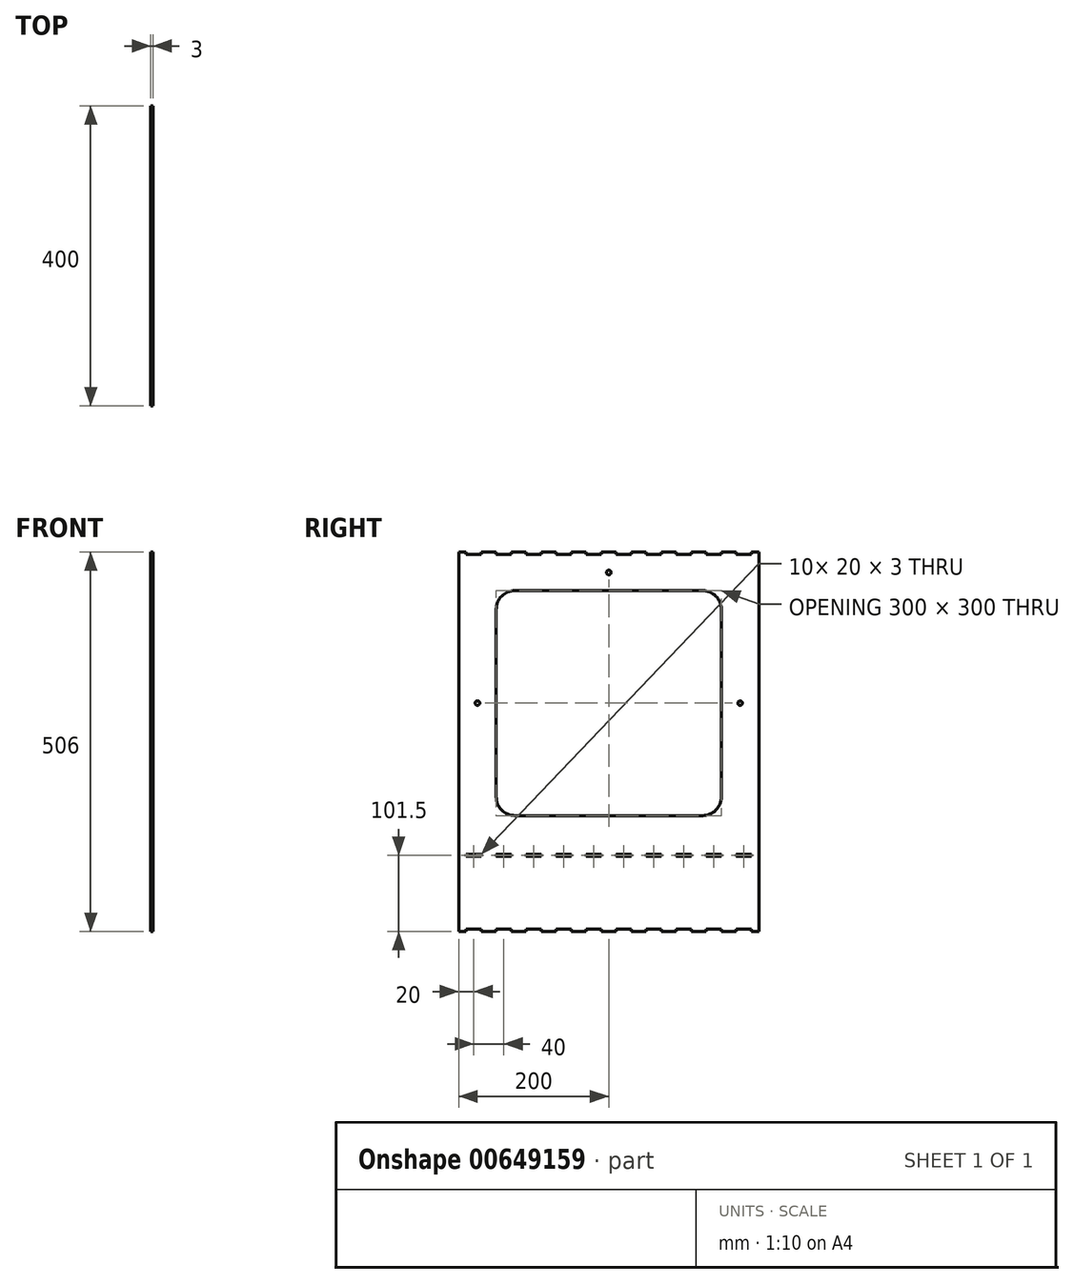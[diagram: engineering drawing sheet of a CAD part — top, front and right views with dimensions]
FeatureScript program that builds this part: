
annotation { "Feature Type Name" : "Feature", "Feature Type Description" : "" }
export const myFeature = defineFeature(function(context is Context, id is Id, definition is map)
    precondition{}
    {
        {
            var Q0;
            Q0=qCreatedBy(makeId("Right.planeOp"),FACE);
            var sketch = newSketch(context, id + "F0", { "sketchPlane" : qUnion([Q0])});
            skLineSegment(sketch, "E0.bottom", {"start": v(200, 250) * mm, "end": v(-200, 250) * mm});
            skLineSegment(sketch, "E0.top", {"start": v(200, -250) * mm, "end": v(-200, -250) * mm});
            skLineSegment(sketch, "E0.left", {"start": v(200, 250) * mm, "end": v(200, -250) * mm});
            skLineSegment(sketch, "E0.right", {"start": v(-200, 250) * mm, "end": v(-200, -250) * mm});
            skPoint(sketch, "E0.middle", {"position": v(0, 0) * mm});
            skSolve(sketch);
        }
        {
            var Q0;
            Q0 = qSketchRegion(id + "F0", true);
            extrude(context, id + "F1", {"entities" : qUnion([Q0]), "depth" : 3 * mm, "offsetDistance" : 25 * mm});
        }
        {
            var Q0;
            Q0=makeQuery(id+"F1.opExtrude","CAP_FACE",FACE,{"disambiguationData":[OSD([sQuery(id+"F0.wireOp",EDGE,"E0.bottom"),sQuery(id+"F0.wireOp",EDGE,"E0.top"),sQuery(id+"F0.wireOp",EDGE,"E0.left"),sQuery(id+"F0.wireOp",EDGE,"E0.right")])],"isStart":false});
            var sketch = newSketch(context, id + "F2", { "sketchPlane" : qUnion([Q0])});
            skLineSegment(sketch, "E1.bottom", {"start": v(-200, 250) * mm, "end": v(-190, 250) * mm});
            skLineSegment(sketch, "E1.top", {"start": v(-200, 253) * mm, "end": v(-190, 253) * mm});
            skLineSegment(sketch, "E1.left", {"start": v(-200, 250) * mm, "end": v(-200, 253) * mm});
            skLineSegment(sketch, "E1.right", {"start": v(-190, 250) * mm, "end": v(-190, 253) * mm});
            skLineSegment(sketch, "E2", {"start": v(-190, 250) * mm, "end": v(-170, 250) * mm, "construction": true});
            skLineSegment(sketch, "E3.bottom", {"start": v(-170, 250) * mm, "end": v(-150, 250) * mm});
            skLineSegment(sketch, "E3.top", {"start": v(-170, 253) * mm, "end": v(-150, 253) * mm});
            skLineSegment(sketch, "E3.left", {"start": v(-170, 250) * mm, "end": v(-170, 253) * mm});
            skLineSegment(sketch, "E3.right", {"start": v(-150, 250) * mm, "end": v(-150, 253) * mm});
            skLineSegment(sketch, "E4.1.0.0", {"start": v(-110, 250) * mm, "end": v(-110, 253) * mm});
            skLineSegment(sketch, "E4.1.0.1", {"start": v(-130, 250) * mm, "end": v(-110, 250) * mm});
            skLineSegment(sketch, "E4.1.0.2", {"start": v(-130, 250) * mm, "end": v(-130, 253) * mm});
            skLineSegment(sketch, "E4.1.0.3", {"start": v(-130, 253) * mm, "end": v(-110, 253) * mm});
            skLineSegment(sketch, "E4.2.0.0", {"start": v(-70, 250) * mm, "end": v(-70, 253) * mm});
            skLineSegment(sketch, "E4.2.0.1", {"start": v(-90, 250) * mm, "end": v(-70, 250) * mm});
            skLineSegment(sketch, "E4.2.0.2", {"start": v(-90, 250) * mm, "end": v(-90, 253) * mm});
            skLineSegment(sketch, "E4.2.0.3", {"start": v(-90, 253) * mm, "end": v(-70, 253) * mm});
            skLineSegment(sketch, "E4.3.0.0", {"start": v(-30, 250) * mm, "end": v(-30, 253) * mm});
            skLineSegment(sketch, "E4.3.0.1", {"start": v(-50, 250) * mm, "end": v(-30, 250) * mm});
            skLineSegment(sketch, "E4.3.0.2", {"start": v(-50, 250) * mm, "end": v(-50, 253) * mm});
            skLineSegment(sketch, "E4.3.0.3", {"start": v(-50, 253) * mm, "end": v(-30, 253) * mm});
            skLineSegment(sketch, "E4.4.0.0", {"start": v(10, 250) * mm, "end": v(10, 253) * mm});
            skLineSegment(sketch, "E4.4.0.1", {"start": v(-10, 250) * mm, "end": v(10, 250) * mm});
            skLineSegment(sketch, "E4.4.0.2", {"start": v(-10, 250) * mm, "end": v(-10, 253) * mm});
            skLineSegment(sketch, "E4.4.0.3", {"start": v(-10, 253) * mm, "end": v(10, 253) * mm});
            skLineSegment(sketch, "E4.5.0.0", {"start": v(50, 250) * mm, "end": v(50, 253) * mm});
            skLineSegment(sketch, "E4.5.0.1", {"start": v(30, 250) * mm, "end": v(50, 250) * mm});
            skLineSegment(sketch, "E4.5.0.2", {"start": v(30, 250) * mm, "end": v(30, 253) * mm});
            skLineSegment(sketch, "E4.5.0.3", {"start": v(30, 253) * mm, "end": v(50, 253) * mm});
            skLineSegment(sketch, "E4.6.0.0", {"start": v(90, 250) * mm, "end": v(90, 253) * mm});
            skLineSegment(sketch, "E4.6.0.1", {"start": v(70, 250) * mm, "end": v(90, 250) * mm});
            skLineSegment(sketch, "E4.6.0.2", {"start": v(70, 250) * mm, "end": v(70, 253) * mm});
            skLineSegment(sketch, "E4.6.0.3", {"start": v(70, 253) * mm, "end": v(90, 253) * mm});
            skLineSegment(sketch, "E4.7.0.0", {"start": v(130, 250) * mm, "end": v(130, 253) * mm});
            skLineSegment(sketch, "E4.7.0.1", {"start": v(110, 250) * mm, "end": v(130, 250) * mm});
            skLineSegment(sketch, "E4.7.0.2", {"start": v(110, 250) * mm, "end": v(110, 253) * mm});
            skLineSegment(sketch, "E4.7.0.3", {"start": v(110, 253) * mm, "end": v(130, 253) * mm});
            skLineSegment(sketch, "E4.8.0.0", {"start": v(170, 250) * mm, "end": v(170, 253) * mm});
            skLineSegment(sketch, "E4.8.0.1", {"start": v(150, 250) * mm, "end": v(170, 250) * mm});
            skLineSegment(sketch, "E4.8.0.2", {"start": v(150, 250) * mm, "end": v(150, 253) * mm});
            skLineSegment(sketch, "E4.8.0.3", {"start": v(150, 253) * mm, "end": v(170, 253) * mm});
            skLineSegment(sketch, "E4.direction1", {"start": v(-170, 250) * mm, "end": v(-130, 250) * mm, "construction": true});
            skLineSegment(sketch, "E5.bottom", {"start": v(200, 250) * mm, "end": v(190, 250) * mm});
            skLineSegment(sketch, "E5.top", {"start": v(200, 253) * mm, "end": v(190, 253) * mm});
            skLineSegment(sketch, "E5.left", {"start": v(200, 250) * mm, "end": v(200, 253) * mm});
            skLineSegment(sketch, "E5.right", {"start": v(190, 250) * mm, "end": v(190, 253) * mm});
            skLineSegment(sketch, "E6.MirrorCS", {"start": v(-190, -250) * mm, "end": v(-190, -253) * mm});
            skLineSegment(sketch, "E7.MirrorCS", {"start": v(-190, -250) * mm, "end": v(-170, -250) * mm, "construction": true});
            skLineSegment(sketch, "E8.MirrorCS", {"start": v(-170, -250) * mm, "end": v(-150, -250) * mm});
            skLineSegment(sketch, "E9.MirrorCS", {"start": v(-170, -253) * mm, "end": v(-150, -253) * mm});
            skLineSegment(sketch, "E10.MirrorCS", {"start": v(-170, -250) * mm, "end": v(-170, -253) * mm});
            skLineSegment(sketch, "E11.MirrorCS", {"start": v(-150, -250) * mm, "end": v(-150, -253) * mm});
            skLineSegment(sketch, "E12.MirrorCS", {"start": v(-130, -250) * mm, "end": v(-130, -253) * mm});
            skLineSegment(sketch, "E13.MirrorCS", {"start": v(200, -250) * mm, "end": v(200, -253) * mm});
            skLineSegment(sketch, "E14.MirrorCS", {"start": v(-90, -250) * mm, "end": v(-90, -253) * mm});
            skLineSegment(sketch, "E15.MirrorCS", {"start": v(-200, -253) * mm, "end": v(-190, -253) * mm});
            skLineSegment(sketch, "E16.MirrorCS", {"start": v(-200, -250) * mm, "end": v(-190, -250) * mm});
            skLineSegment(sketch, "E17.MirrorCS", {"start": v(-200, -250) * mm, "end": v(-200, -253) * mm});
            skLineSegment(sketch, "E18.MirrorCS", {"start": v(-130, -253) * mm, "end": v(-110, -253) * mm});
            skLineSegment(sketch, "E19.MirrorCS", {"start": v(-110, -250) * mm, "end": v(-110, -253) * mm});
            skLineSegment(sketch, "E20.MirrorCS", {"start": v(-130, -250) * mm, "end": v(-110, -250) * mm});
            skLineSegment(sketch, "E21.MirrorCS", {"start": v(200, -253) * mm, "end": v(190, -253) * mm});
            skLineSegment(sketch, "E22.MirrorCS", {"start": v(150, -250) * mm, "end": v(150, -253) * mm});
            skLineSegment(sketch, "E23.MirrorCS", {"start": v(-10, -250) * mm, "end": v(-10, -253) * mm});
            skLineSegment(sketch, "E24.MirrorCS", {"start": v(190, -250) * mm, "end": v(190, -253) * mm});
            skLineSegment(sketch, "E25.MirrorCS", {"start": v(-90, -253) * mm, "end": v(-70, -253) * mm});
            skLineSegment(sketch, "E26.MirrorCS", {"start": v(170, -250) * mm, "end": v(170, -253) * mm});
            skLineSegment(sketch, "E27.MirrorCS", {"start": v(10, -250) * mm, "end": v(10, -253) * mm});
            skLineSegment(sketch, "E28.MirrorCS", {"start": v(130, -250) * mm, "end": v(130, -253) * mm});
            skLineSegment(sketch, "E29.MirrorCS", {"start": v(-30, -250) * mm, "end": v(-30, -253) * mm});
            skLineSegment(sketch, "E30.MirrorCS", {"start": v(-90, -250) * mm, "end": v(-70, -250) * mm});
            skLineSegment(sketch, "E31.MirrorCS", {"start": v(-170, -250) * mm, "end": v(-130, -250) * mm, "construction": true});
            skLineSegment(sketch, "E32.MirrorCS", {"start": v(200, -250) * mm, "end": v(190, -250) * mm});
            skLineSegment(sketch, "E33.MirrorCS", {"start": v(30, -250) * mm, "end": v(30, -253) * mm});
            skLineSegment(sketch, "E34.MirrorCS", {"start": v(90, -250) * mm, "end": v(90, -253) * mm});
            skLineSegment(sketch, "E35.MirrorCS", {"start": v(110, -253) * mm, "end": v(130, -253) * mm});
            skLineSegment(sketch, "E36.MirrorCS", {"start": v(-50, -253) * mm, "end": v(-30, -253) * mm});
            skLineSegment(sketch, "E37.MirrorCS", {"start": v(70, -253) * mm, "end": v(90, -253) * mm});
            skLineSegment(sketch, "E38.MirrorCS", {"start": v(150, -253) * mm, "end": v(170, -253) * mm});
            skLineSegment(sketch, "E39.MirrorCS", {"start": v(30, -253) * mm, "end": v(50, -253) * mm});
            skLineSegment(sketch, "E40.MirrorCS", {"start": v(-10, -253) * mm, "end": v(10, -253) * mm});
            skLineSegment(sketch, "E41.MirrorCS", {"start": v(70, -250) * mm, "end": v(90, -250) * mm});
            skLineSegment(sketch, "E42.MirrorCS", {"start": v(-70, -250) * mm, "end": v(-70, -253) * mm});
            skLineSegment(sketch, "E43.MirrorCS", {"start": v(-50, -250) * mm, "end": v(-50, -253) * mm});
            skLineSegment(sketch, "E44.MirrorCS", {"start": v(150, -250) * mm, "end": v(170, -250) * mm});
            skLineSegment(sketch, "E45.MirrorCS", {"start": v(70, -250) * mm, "end": v(70, -253) * mm});
            skLineSegment(sketch, "E46.MirrorCS", {"start": v(-10, -250) * mm, "end": v(10, -250) * mm});
            skLineSegment(sketch, "E47.MirrorCS", {"start": v(110, -250) * mm, "end": v(130, -250) * mm});
            skLineSegment(sketch, "E48.MirrorCS", {"start": v(-50, -250) * mm, "end": v(-30, -250) * mm});
            skLineSegment(sketch, "E49.MirrorCS", {"start": v(50, -250) * mm, "end": v(50, -253) * mm});
            skLineSegment(sketch, "E50.MirrorCS", {"start": v(30, -250) * mm, "end": v(50, -250) * mm});
            skLineSegment(sketch, "E51.MirrorCS", {"start": v(110, -250) * mm, "end": v(110, -253) * mm});
            skSolve(sketch);
        }
        {
            var Q0;
            Q0 = qSketchRegion(id + "F2", true);
            var Q1;
            Q1=makeQuery(id+"F1.opExtrude","CAP_FACE",FACE,{"disambiguationData":[OSD([sQuery(id+"F0.wireOp",EDGE,"E0.bottom"),sQuery(id+"F0.wireOp",EDGE,"E0.top"),sQuery(id+"F0.wireOp",EDGE,"E0.left"),sQuery(id+"F0.wireOp",EDGE,"E0.right")])],"isStart":true});
            extrude(context, id + "F3", {"entities" : qUnion([Q0]), "operationType" : NewBodyOperationType.ADD, "endBound" : BoundingType.UP_TO_SURFACE, "oppositeDirection" : true, "depth" : 25 * mm, "endBoundEntityFace" : qUnion([Q1]), "offsetDistance" : 25 * mm});
        }
        {
            var Q0;
            {var subQ0=sQuery(id+"F0.wireOp",EDGE,"E0.right");var subQ1=sQuery(id+"F0.wireOp",EDGE,"E0.left");var subQ2=sQuery(id+"F0.wireOp",EDGE,"E0.top");var subQ3=sQuery(id+"F0.wireOp",EDGE,"E0.bottom");Q0=makeQuery(id+"F3.boolean.opBoolean","MERGE",FACE,{"derivedFrom":[makeQuery(id+"F1.opExtrude","CAP_FACE",FACE,{"disambiguationData":[OSD([subQ3,subQ2,subQ1,subQ0])],"isStart":true}),makeQuery(id+"F3.opExtrude","CAP_FACE",FACE,{"disambiguationData":[OSD([subQ3,subQ2,subQ1,subQ0]),OD(0.0)],"isStart":false}),makeQuery(id+"F3.opExtrude","CAP_FACE",FACE,{"disambiguationData":[OSD([subQ3,subQ2,subQ1,subQ0]),OD(1.0)],"isStart":false}),makeQuery(id+"F3.opExtrude","CAP_FACE",FACE,{"disambiguationData":[OSD([subQ3,subQ2,subQ1,subQ0]),OD(2.0)],"isStart":false}),makeQuery(id+"F3.opExtrude","CAP_FACE",FACE,{"disambiguationData":[OSD([subQ3,subQ2,subQ1,subQ0]),OD(3.0)],"isStart":false}),makeQuery(id+"F3.opExtrude","CAP_FACE",FACE,{"disambiguationData":[OSD([subQ3,subQ2,subQ1,subQ0]),OD(4.0)],"isStart":false}),makeQuery(id+"F3.opExtrude","CAP_FACE",FACE,{"disambiguationData":[OSD([subQ3,subQ2,subQ1,subQ0]),OD(5.0)],"isStart":false}),makeQuery(id+"F3.opExtrude","CAP_FACE",FACE,{"disambiguationData":[OSD([subQ3,subQ2,subQ1,subQ0]),OD(6.0)],"isStart":false}),makeQuery(id+"F3.opExtrude","CAP_FACE",FACE,{"disambiguationData":[OSD([subQ3,subQ2,subQ1,subQ0]),OD(7.0)],"isStart":false}),makeQuery(id+"F3.opExtrude","CAP_FACE",FACE,{"disambiguationData":[OSD([subQ3,subQ2,subQ1,subQ0]),OD(8.0)],"isStart":false}),makeQuery(id+"F3.opExtrude","CAP_FACE",FACE,{"disambiguationData":[OSD([subQ3,subQ2,subQ1,subQ0]),OD(9.0)],"isStart":false}),makeQuery(id+"F3.opExtrude","CAP_FACE",FACE,{"disambiguationData":[OSD([subQ3,subQ2,subQ1,subQ0]),OD(10.0)],"isStart":false}),makeQuery(id+"F3.opExtrude","CAP_FACE",FACE,{"disambiguationData":[OSD([subQ3,subQ2,subQ1,subQ0]),OD(11.0)],"isStart":false}),makeQuery(id+"F3.opExtrude","CAP_FACE",FACE,{"disambiguationData":[OSD([subQ3,subQ2,subQ1,subQ0]),OD(12.0)],"isStart":false}),makeQuery(id+"F3.opExtrude","CAP_FACE",FACE,{"disambiguationData":[OSD([subQ3,subQ2,subQ1,subQ0]),OD(13.0)],"isStart":false}),makeQuery(id+"F3.opExtrude","CAP_FACE",FACE,{"disambiguationData":[OSD([subQ3,subQ2,subQ1,subQ0]),OD(14.0)],"isStart":false}),makeQuery(id+"F3.opExtrude","CAP_FACE",FACE,{"disambiguationData":[OSD([subQ3,subQ2,subQ1,subQ0]),OD(15.0)],"isStart":false}),makeQuery(id+"F3.opExtrude","CAP_FACE",FACE,{"disambiguationData":[OSD([subQ3,subQ2,subQ1,subQ0]),OD(16.0)],"isStart":false}),makeQuery(id+"F3.opExtrude","CAP_FACE",FACE,{"disambiguationData":[OSD([subQ3,subQ2,subQ1,subQ0]),OD(17.0)],"isStart":false}),makeQuery(id+"F3.opExtrude","CAP_FACE",FACE,{"disambiguationData":[OSD([subQ3,subQ2,subQ1,subQ0]),OD(18.0)],"isStart":false}),makeQuery(id+"F3.opExtrude","CAP_FACE",FACE,{"disambiguationData":[OSD([subQ3,subQ2,subQ1,subQ0]),OD(19.0)],"isStart":false}),makeQuery(id+"F3.opExtrude","CAP_FACE",FACE,{"disambiguationData":[OSD([subQ3,subQ2,subQ1,subQ0]),OD(20.0)],"isStart":false}),makeQuery(id+"F3.opExtrude","CAP_FACE",FACE,{"disambiguationData":[OSD([subQ3,subQ2,subQ1,subQ0]),OD(21.0)],"isStart":false})]});}
            var sketch = newSketch(context, id + "F4", { "sketchPlane" : qUnion([Q0])});
            skLineSegment(sketch, "E52", {"start": v(-200, 253) * mm, "end": v(-200, -153) * mm, "construction": true});
            skLineSegment(sketch, "E53", {"start": v(-200, -153) * mm, "end": v(-190, -153) * mm, "construction": true});
            skLineSegment(sketch, "E54.bottom", {"start": v(-190, -153) * mm, "end": v(-170, -153) * mm});
            skLineSegment(sketch, "E54.top", {"start": v(-190, -150) * mm, "end": v(-170, -150) * mm});
            skLineSegment(sketch, "E54.left", {"start": v(-190, -153) * mm, "end": v(-190, -150) * mm});
            skLineSegment(sketch, "E54.right", {"start": v(-170, -153) * mm, "end": v(-170, -150) * mm});
            skLineSegment(sketch, "E55.1.0.0", {"start": v(-150, -150) * mm, "end": v(-130, -150) * mm});
            skLineSegment(sketch, "E55.1.0.1", {"start": v(-150, -153) * mm, "end": v(-130, -153) * mm});
            skLineSegment(sketch, "E55.1.0.2", {"start": v(-130, -153) * mm, "end": v(-130, -150) * mm});
            skLineSegment(sketch, "E55.2.0.0", {"start": v(-110, -150) * mm, "end": v(-90, -150) * mm});
            skLineSegment(sketch, "E55.2.0.1", {"start": v(-110, -153) * mm, "end": v(-90, -153) * mm});
            skLineSegment(sketch, "E55.2.0.2", {"start": v(-90, -153) * mm, "end": v(-90, -150) * mm});
            skLineSegment(sketch, "E55.3.0.0", {"start": v(-70, -150) * mm, "end": v(-50, -150) * mm});
            skLineSegment(sketch, "E55.3.0.1", {"start": v(-70, -153) * mm, "end": v(-50, -153) * mm});
            skLineSegment(sketch, "E55.3.0.2", {"start": v(-50, -153) * mm, "end": v(-50, -150) * mm});
            skLineSegment(sketch, "E55.4.0.0", {"start": v(-30, -150) * mm, "end": v(-10, -150) * mm});
            skLineSegment(sketch, "E55.4.0.1", {"start": v(-30, -153) * mm, "end": v(-10, -153) * mm});
            skLineSegment(sketch, "E55.4.0.2", {"start": v(-10, -153) * mm, "end": v(-10, -150) * mm});
            skLineSegment(sketch, "E55.5.0.0", {"start": v(10, -150) * mm, "end": v(30, -150) * mm});
            skLineSegment(sketch, "E55.5.0.1", {"start": v(10, -153) * mm, "end": v(30, -153) * mm});
            skLineSegment(sketch, "E55.5.0.2", {"start": v(30, -153) * mm, "end": v(30, -150) * mm});
            skLineSegment(sketch, "E55.6.0.0", {"start": v(50, -150) * mm, "end": v(70, -150) * mm});
            skLineSegment(sketch, "E55.6.0.1", {"start": v(50, -153) * mm, "end": v(70, -153) * mm});
            skLineSegment(sketch, "E55.6.0.2", {"start": v(70, -153) * mm, "end": v(70, -150) * mm});
            skLineSegment(sketch, "E55.7.0.0", {"start": v(90, -150) * mm, "end": v(110, -150) * mm});
            skLineSegment(sketch, "E55.7.0.1", {"start": v(90, -153) * mm, "end": v(110, -153) * mm});
            skLineSegment(sketch, "E55.7.0.2", {"start": v(110, -153) * mm, "end": v(110, -150) * mm});
            skLineSegment(sketch, "E55.8.0.0", {"start": v(130, -150) * mm, "end": v(150, -150) * mm});
            skLineSegment(sketch, "E55.8.0.1", {"start": v(130, -153) * mm, "end": v(150, -153) * mm});
            skLineSegment(sketch, "E55.8.0.2", {"start": v(150, -153) * mm, "end": v(150, -150) * mm});
            skLineSegment(sketch, "E55.9.0.0", {"start": v(170, -150) * mm, "end": v(190, -150) * mm});
            skLineSegment(sketch, "E55.9.0.1", {"start": v(170, -153) * mm, "end": v(190, -153) * mm});
            skLineSegment(sketch, "E55.9.0.2", {"start": v(190, -153) * mm, "end": v(190, -150) * mm});
            skLineSegment(sketch, "E55.direction1", {"start": v(-190, -150) * mm, "end": v(-150, -150) * mm, "construction": true});
            skLineSegment(sketch, "E56.1.0.0", {"start": v(-150, -153) * mm, "end": v(-150, -150) * mm});
            skLineSegment(sketch, "E56.2.0.0", {"start": v(-110, -153) * mm, "end": v(-110, -150) * mm});
            skLineSegment(sketch, "E56.3.0.0", {"start": v(-70, -153) * mm, "end": v(-70, -150) * mm});
            skLineSegment(sketch, "E56.4.0.0", {"start": v(-30, -153) * mm, "end": v(-30, -150) * mm});
            skLineSegment(sketch, "E56.5.0.0", {"start": v(10, -153) * mm, "end": v(10, -150) * mm});
            skLineSegment(sketch, "E56.6.0.0", {"start": v(50, -153) * mm, "end": v(50, -150) * mm});
            skLineSegment(sketch, "E56.7.0.0", {"start": v(90, -153) * mm, "end": v(90, -150) * mm});
            skLineSegment(sketch, "E56.8.0.0", {"start": v(130, -153) * mm, "end": v(130, -150) * mm});
            skLineSegment(sketch, "E56.9.0.0", {"start": v(170, -153) * mm, "end": v(170, -150) * mm});
            skLineSegment(sketch, "E56.direction1", {"start": v(-190, -153) * mm, "end": v(-150, -153) * mm, "construction": true});
            skSolve(sketch);
        }
        {
            var Q0;
            Q0 = qSketchRegion(id + "F4", true);
            extrude(context, id + "F5", {"entities" : qUnion([Q0]), "operationType" : NewBodyOperationType.REMOVE, "endBound" : BoundingType.THROUGH_ALL, "oppositeDirection" : true, "depth" : 25 * mm, "offsetDistance" : 25 * mm});
        }
        {
            var Q0;
            {var subQ0=sQuery(id+"F0.wireOp",EDGE,"E0.right");var subQ1=sQuery(id+"F0.wireOp",EDGE,"E0.left");var subQ2=sQuery(id+"F0.wireOp",EDGE,"E0.top");var subQ3=sQuery(id+"F0.wireOp",EDGE,"E0.bottom");Q0=makeQuery(id+"F3.boolean.opBoolean","MERGE",FACE,{"derivedFrom":[makeQuery(id+"F1.opExtrude","CAP_FACE",FACE,{"disambiguationData":[OSD([subQ3,subQ2,subQ1,subQ0])],"isStart":true}),makeQuery(id+"F3.opExtrude","CAP_FACE",FACE,{"disambiguationData":[OSD([subQ3,subQ2,subQ1,subQ0]),OD(0.0)],"isStart":false}),makeQuery(id+"F3.opExtrude","CAP_FACE",FACE,{"disambiguationData":[OSD([subQ3,subQ2,subQ1,subQ0]),OD(1.0)],"isStart":false}),makeQuery(id+"F3.opExtrude","CAP_FACE",FACE,{"disambiguationData":[OSD([subQ3,subQ2,subQ1,subQ0]),OD(2.0)],"isStart":false}),makeQuery(id+"F3.opExtrude","CAP_FACE",FACE,{"disambiguationData":[OSD([subQ3,subQ2,subQ1,subQ0]),OD(3.0)],"isStart":false}),makeQuery(id+"F3.opExtrude","CAP_FACE",FACE,{"disambiguationData":[OSD([subQ3,subQ2,subQ1,subQ0]),OD(4.0)],"isStart":false}),makeQuery(id+"F3.opExtrude","CAP_FACE",FACE,{"disambiguationData":[OSD([subQ3,subQ2,subQ1,subQ0]),OD(5.0)],"isStart":false}),makeQuery(id+"F3.opExtrude","CAP_FACE",FACE,{"disambiguationData":[OSD([subQ3,subQ2,subQ1,subQ0]),OD(6.0)],"isStart":false}),makeQuery(id+"F3.opExtrude","CAP_FACE",FACE,{"disambiguationData":[OSD([subQ3,subQ2,subQ1,subQ0]),OD(7.0)],"isStart":false}),makeQuery(id+"F3.opExtrude","CAP_FACE",FACE,{"disambiguationData":[OSD([subQ3,subQ2,subQ1,subQ0]),OD(8.0)],"isStart":false}),makeQuery(id+"F3.opExtrude","CAP_FACE",FACE,{"disambiguationData":[OSD([subQ3,subQ2,subQ1,subQ0]),OD(9.0)],"isStart":false}),makeQuery(id+"F3.opExtrude","CAP_FACE",FACE,{"disambiguationData":[OSD([subQ3,subQ2,subQ1,subQ0]),OD(10.0)],"isStart":false}),makeQuery(id+"F3.opExtrude","CAP_FACE",FACE,{"disambiguationData":[OSD([subQ3,subQ2,subQ1,subQ0]),OD(11.0)],"isStart":false}),makeQuery(id+"F3.opExtrude","CAP_FACE",FACE,{"disambiguationData":[OSD([subQ3,subQ2,subQ1,subQ0]),OD(12.0)],"isStart":false}),makeQuery(id+"F3.opExtrude","CAP_FACE",FACE,{"disambiguationData":[OSD([subQ3,subQ2,subQ1,subQ0]),OD(13.0)],"isStart":false}),makeQuery(id+"F3.opExtrude","CAP_FACE",FACE,{"disambiguationData":[OSD([subQ3,subQ2,subQ1,subQ0]),OD(14.0)],"isStart":false}),makeQuery(id+"F3.opExtrude","CAP_FACE",FACE,{"disambiguationData":[OSD([subQ3,subQ2,subQ1,subQ0]),OD(15.0)],"isStart":false}),makeQuery(id+"F3.opExtrude","CAP_FACE",FACE,{"disambiguationData":[OSD([subQ3,subQ2,subQ1,subQ0]),OD(16.0)],"isStart":false}),makeQuery(id+"F3.opExtrude","CAP_FACE",FACE,{"disambiguationData":[OSD([subQ3,subQ2,subQ1,subQ0]),OD(17.0)],"isStart":false}),makeQuery(id+"F3.opExtrude","CAP_FACE",FACE,{"disambiguationData":[OSD([subQ3,subQ2,subQ1,subQ0]),OD(18.0)],"isStart":false}),makeQuery(id+"F3.opExtrude","CAP_FACE",FACE,{"disambiguationData":[OSD([subQ3,subQ2,subQ1,subQ0]),OD(19.0)],"isStart":false}),makeQuery(id+"F3.opExtrude","CAP_FACE",FACE,{"disambiguationData":[OSD([subQ3,subQ2,subQ1,subQ0]),OD(20.0)],"isStart":false}),makeQuery(id+"F3.opExtrude","CAP_FACE",FACE,{"disambiguationData":[OSD([subQ3,subQ2,subQ1,subQ0]),OD(21.0)],"isStart":false})]});}
            var sketch = newSketch(context, id + "F6", { "sketchPlane" : qUnion([Q0])});
            skLineSegment(sketch, "E57", {"start": v(0, 253) * mm, "end": v(0, -150) * mm, "construction": true});
            skLineSegment(sketch, "E58.bottom", {"start": v(150, 201.5) * mm, "end": v(-150, 201.5) * mm});
            skLineSegment(sketch, "E58.top", {"start": v(150, -98.5) * mm, "end": v(-150, -98.5) * mm});
            skLineSegment(sketch, "E58.left", {"start": v(150, 201.5) * mm, "end": v(150, -98.5) * mm});
            skLineSegment(sketch, "E58.right", {"start": v(-150, 201.5) * mm, "end": v(-150, -98.5) * mm});
            skPoint(sketch, "E58.middle", {"position": v(0, 51.5) * mm});
            skSolve(sketch);
        }
        {
            var Q0;
            Q0 = qSketchRegion(id + "F6", true);
            extrude(context, id + "F7", {"entities" : qUnion([Q0]), "operationType" : NewBodyOperationType.REMOVE, "oppositeDirection" : true, "depth" : 25 * mm, "offsetDistance" : 25 * mm});
        }
        {
            var Q0;
            Q0=makeQuery(id+"F7.boolean.opBoolean","COPY",EDGE,{"derivedFrom":makeQuery(id+"F7.opExtrude","SWEPT_EDGE",EDGE,{"disambiguationData":[OSD([sQuery(id+"F6.wireOp",EDGE,"E58.bottom"),sQuery(id+"F6.wireOp",EDGE,"E58.right")])]})});
            var Q1;
            Q1=makeQuery(id+"F7.boolean.opBoolean","COPY",EDGE,{"derivedFrom":makeQuery(id+"F7.opExtrude","SWEPT_EDGE",EDGE,{"disambiguationData":[OSD([sQuery(id+"F6.wireOp",EDGE,"E58.bottom"),sQuery(id+"F6.wireOp",EDGE,"E58.left")])]})});
            var Q2;
            Q2=makeQuery(id+"F7.boolean.opBoolean","COPY",EDGE,{"derivedFrom":makeQuery(id+"F7.opExtrude","SWEPT_EDGE",EDGE,{"disambiguationData":[OSD([sQuery(id+"F6.wireOp",EDGE,"E58.top"),sQuery(id+"F6.wireOp",EDGE,"E58.left")])]})});
            var Q3;
            Q3=makeQuery(id+"F7.boolean.opBoolean","COPY",EDGE,{"derivedFrom":makeQuery(id+"F7.opExtrude","SWEPT_EDGE",EDGE,{"disambiguationData":[OSD([sQuery(id+"F6.wireOp",EDGE,"E58.top"),sQuery(id+"F6.wireOp",EDGE,"E58.right")])]})});
            fillet(context, id + "F8", {"entities" : qUnion([Q0, Q1, Q2, Q3]), "radius" : 25 * mm, "tangentPropagation" : true, "allowEdgeOverflow" : false});
        }
        {
            var Q0;
            Q0=makeQuery(id+"F3.boolean.opBoolean","MERGE",FACE,{"derivedFrom":[makeQuery(id+"F1.opExtrude","CAP_FACE",FACE,{"disambiguationData":[OSD([sQuery(id+"F0.wireOp",EDGE,"E0.bottom"),sQuery(id+"F0.wireOp",EDGE,"E0.top"),sQuery(id+"F0.wireOp",EDGE,"E0.left"),sQuery(id+"F0.wireOp",EDGE,"E0.right")])],"isStart":false}),makeQuery(id+"F3.opExtrude","CAP_FACE",FACE,{"disambiguationData":[OSD([sQuery(id+"F2.wireOp",EDGE,"E1.bottom"),sQuery(id+"F2.wireOp",EDGE,"E1.top"),sQuery(id+"F2.wireOp",EDGE,"E1.left"),sQuery(id+"F2.wireOp",EDGE,"E1.right")])],"isStart":true}),makeQuery(id+"F3.opExtrude","CAP_FACE",FACE,{"disambiguationData":[OSD([sQuery(id+"F2.wireOp",EDGE,"E3.bottom"),sQuery(id+"F2.wireOp",EDGE,"E3.top"),sQuery(id+"F2.wireOp",EDGE,"E3.left"),sQuery(id+"F2.wireOp",EDGE,"E3.right")])],"isStart":true}),makeQuery(id+"F3.opExtrude","CAP_FACE",FACE,{"disambiguationData":[OSD([sQuery(id+"F2.wireOp",EDGE,"E4.1.0.0"),sQuery(id+"F2.wireOp",EDGE,"E4.1.0.1"),sQuery(id+"F2.wireOp",EDGE,"E4.1.0.2"),sQuery(id+"F2.wireOp",EDGE,"E4.1.0.3")])],"isStart":true}),makeQuery(id+"F3.opExtrude","CAP_FACE",FACE,{"disambiguationData":[OSD([sQuery(id+"F2.wireOp",EDGE,"E4.2.0.0"),sQuery(id+"F2.wireOp",EDGE,"E4.2.0.1"),sQuery(id+"F2.wireOp",EDGE,"E4.2.0.2"),sQuery(id+"F2.wireOp",EDGE,"E4.2.0.3")])],"isStart":true}),makeQuery(id+"F3.opExtrude","CAP_FACE",FACE,{"disambiguationData":[OSD([sQuery(id+"F2.wireOp",EDGE,"E4.3.0.0"),sQuery(id+"F2.wireOp",EDGE,"E4.3.0.1"),sQuery(id+"F2.wireOp",EDGE,"E4.3.0.2"),sQuery(id+"F2.wireOp",EDGE,"E4.3.0.3")])],"isStart":true}),makeQuery(id+"F3.opExtrude","CAP_FACE",FACE,{"disambiguationData":[OSD([sQuery(id+"F2.wireOp",EDGE,"E4.4.0.0"),sQuery(id+"F2.wireOp",EDGE,"E4.4.0.1"),sQuery(id+"F2.wireOp",EDGE,"E4.4.0.2"),sQuery(id+"F2.wireOp",EDGE,"E4.4.0.3")])],"isStart":true}),makeQuery(id+"F3.opExtrude","CAP_FACE",FACE,{"disambiguationData":[OSD([sQuery(id+"F2.wireOp",EDGE,"E4.5.0.0"),sQuery(id+"F2.wireOp",EDGE,"E4.5.0.1"),sQuery(id+"F2.wireOp",EDGE,"E4.5.0.2"),sQuery(id+"F2.wireOp",EDGE,"E4.5.0.3")])],"isStart":true}),makeQuery(id+"F3.opExtrude","CAP_FACE",FACE,{"disambiguationData":[OSD([sQuery(id+"F2.wireOp",EDGE,"E4.6.0.0"),sQuery(id+"F2.wireOp",EDGE,"E4.6.0.1"),sQuery(id+"F2.wireOp",EDGE,"E4.6.0.2"),sQuery(id+"F2.wireOp",EDGE,"E4.6.0.3")])],"isStart":true}),makeQuery(id+"F3.opExtrude","CAP_FACE",FACE,{"disambiguationData":[OSD([sQuery(id+"F2.wireOp",EDGE,"E4.7.0.0"),sQuery(id+"F2.wireOp",EDGE,"E4.7.0.1"),sQuery(id+"F2.wireOp",EDGE,"E4.7.0.2"),sQuery(id+"F2.wireOp",EDGE,"E4.7.0.3")])],"isStart":true}),makeQuery(id+"F3.opExtrude","CAP_FACE",FACE,{"disambiguationData":[OSD([sQuery(id+"F2.wireOp",EDGE,"E4.8.0.0"),sQuery(id+"F2.wireOp",EDGE,"E4.8.0.1"),sQuery(id+"F2.wireOp",EDGE,"E4.8.0.2"),sQuery(id+"F2.wireOp",EDGE,"E4.8.0.3")])],"isStart":true}),makeQuery(id+"F3.opExtrude","CAP_FACE",FACE,{"disambiguationData":[OSD([sQuery(id+"F2.wireOp",EDGE,"E5.bottom"),sQuery(id+"F2.wireOp",EDGE,"E5.top"),sQuery(id+"F2.wireOp",EDGE,"E5.left"),sQuery(id+"F2.wireOp",EDGE,"E5.right")])],"isStart":true}),makeQuery(id+"F3.opExtrude","CAP_FACE",FACE,{"disambiguationData":[OSD([sQuery(id+"F2.wireOp",EDGE,"E6.MirrorCS"),sQuery(id+"F2.wireOp",EDGE,"E15.MirrorCS"),sQuery(id+"F2.wireOp",EDGE,"E16.MirrorCS"),sQuery(id+"F2.wireOp",EDGE,"E17.MirrorCS")])],"isStart":true}),makeQuery(id+"F3.opExtrude","CAP_FACE",FACE,{"disambiguationData":[OSD([sQuery(id+"F2.wireOp",EDGE,"E8.MirrorCS"),sQuery(id+"F2.wireOp",EDGE,"E9.MirrorCS"),sQuery(id+"F2.wireOp",EDGE,"E10.MirrorCS"),sQuery(id+"F2.wireOp",EDGE,"E11.MirrorCS")])],"isStart":true}),makeQuery(id+"F3.opExtrude","CAP_FACE",FACE,{"disambiguationData":[OSD([sQuery(id+"F2.wireOp",EDGE,"E12.MirrorCS"),sQuery(id+"F2.wireOp",EDGE,"E18.MirrorCS"),sQuery(id+"F2.wireOp",EDGE,"E19.MirrorCS"),sQuery(id+"F2.wireOp",EDGE,"E20.MirrorCS")])],"isStart":true}),makeQuery(id+"F3.opExtrude","CAP_FACE",FACE,{"disambiguationData":[OSD([sQuery(id+"F2.wireOp",EDGE,"E13.MirrorCS"),sQuery(id+"F2.wireOp",EDGE,"E21.MirrorCS"),sQuery(id+"F2.wireOp",EDGE,"E24.MirrorCS"),sQuery(id+"F2.wireOp",EDGE,"E32.MirrorCS")])],"isStart":true}),makeQuery(id+"F3.opExtrude","CAP_FACE",FACE,{"disambiguationData":[OSD([sQuery(id+"F2.wireOp",EDGE,"E14.MirrorCS"),sQuery(id+"F2.wireOp",EDGE,"E25.MirrorCS"),sQuery(id+"F2.wireOp",EDGE,"E30.MirrorCS"),sQuery(id+"F2.wireOp",EDGE,"E42.MirrorCS")])],"isStart":true}),makeQuery(id+"F3.opExtrude","CAP_FACE",FACE,{"disambiguationData":[OSD([sQuery(id+"F2.wireOp",EDGE,"E22.MirrorCS"),sQuery(id+"F2.wireOp",EDGE,"E26.MirrorCS"),sQuery(id+"F2.wireOp",EDGE,"E38.MirrorCS"),sQuery(id+"F2.wireOp",EDGE,"E44.MirrorCS")])],"isStart":true}),makeQuery(id+"F3.opExtrude","CAP_FACE",FACE,{"disambiguationData":[OSD([sQuery(id+"F2.wireOp",EDGE,"E23.MirrorCS"),sQuery(id+"F2.wireOp",EDGE,"E27.MirrorCS"),sQuery(id+"F2.wireOp",EDGE,"E40.MirrorCS"),sQuery(id+"F2.wireOp",EDGE,"E46.MirrorCS")])],"isStart":true}),makeQuery(id+"F3.opExtrude","CAP_FACE",FACE,{"disambiguationData":[OSD([sQuery(id+"F2.wireOp",EDGE,"E28.MirrorCS"),sQuery(id+"F2.wireOp",EDGE,"E35.MirrorCS"),sQuery(id+"F2.wireOp",EDGE,"E47.MirrorCS"),sQuery(id+"F2.wireOp",EDGE,"E51.MirrorCS")])],"isStart":true}),makeQuery(id+"F3.opExtrude","CAP_FACE",FACE,{"disambiguationData":[OSD([sQuery(id+"F2.wireOp",EDGE,"E29.MirrorCS"),sQuery(id+"F2.wireOp",EDGE,"E36.MirrorCS"),sQuery(id+"F2.wireOp",EDGE,"E43.MirrorCS"),sQuery(id+"F2.wireOp",EDGE,"E48.MirrorCS")])],"isStart":true}),makeQuery(id+"F3.opExtrude","CAP_FACE",FACE,{"disambiguationData":[OSD([sQuery(id+"F2.wireOp",EDGE,"E33.MirrorCS"),sQuery(id+"F2.wireOp",EDGE,"E39.MirrorCS"),sQuery(id+"F2.wireOp",EDGE,"E49.MirrorCS"),sQuery(id+"F2.wireOp",EDGE,"E50.MirrorCS")])],"isStart":true}),makeQuery(id+"F3.opExtrude","CAP_FACE",FACE,{"disambiguationData":[OSD([sQuery(id+"F2.wireOp",EDGE,"E34.MirrorCS"),sQuery(id+"F2.wireOp",EDGE,"E37.MirrorCS"),sQuery(id+"F2.wireOp",EDGE,"E41.MirrorCS"),sQuery(id+"F2.wireOp",EDGE,"E45.MirrorCS")])],"isStart":true})]});
            var sketch = newSketch(context, id + "F9", { "sketchPlane" : qUnion([Q0])});
            skLineSegment(sketch, "E59", {"start": v(0, 201.5) * mm, "end": v(0, 250) * mm, "construction": true});
            skCircle(sketch, "E60", {"center": v(0, 225.75) * mm, "radius": 3 * mm});
            skLineSegment(sketch, "E61", {"start": v(-150, 51.5) * mm, "end": v(-200, 51.5) * mm, "construction": true});
            skCircle(sketch, "E62", {"center": v(-175, 51.5) * mm, "radius": 3 * mm});
            skLineSegment(sketch, "E63", {"start": v(150, 51.5) * mm, "end": v(200, 51.5) * mm, "construction": true});
            skCircle(sketch, "E64", {"center": v(175, 51.5) * mm, "radius": 3 * mm});
            skSolve(sketch);
        }
        {
            var Q0;
            Q0 = qSketchRegion(id + "F9", true);
            extrude(context, id + "F10", {"entities" : qUnion([Q0]), "operationType" : NewBodyOperationType.REMOVE, "oppositeDirection" : true, "depth" : 25 * mm, "offsetDistance" : 25 * mm});
        }
    });
